# Revit family: Geberit Bambini WC sedište za decu_PRO_450219
name_source: partatom
category: Furniture
revit_build: Autodesk Revit 2018 (Build: 20190510_1515(x64)
units: mm (PartAtom-declared; Revit-internal decimal feet)

## family parameters
Always vertical = Yes
Cut with Voids When Loaded = No
OmniClass Number = 23.40.20.21
OmniClass Title = Toilet and Bath Specialties
Room Calculation Point = Yes
Shared = No
Work Plane-Based = No

## types (2) — shared parameters
BIM datoteka, datum izmene = 2020.05.18
BIM datoteka, proizvođač = Geberit
BIM datoteka, verzija = GEB MG 1.2
CW Connection = Yes
Description = Geberit Bambini WC sedište za decu
GEB_culture = sr-RS
GEB_generic_description = GBC
GEB_generic_manufacturer = generic
GEB_pimversion = 22.02.12
GEB_processing_type = T
GEB_reference = PRO_450219
GEB_translations = {"ATT_10673":"EAN code basic data","ATT_459792":"Boja / površina","applicationPurposes":"Namene","application_range":"Oblast primene","brandName":"Robna marka","characteristics":"Svojstva","content_creator":"BIM datoteka, proizvođač","content_date_changed":"BIM datoteka, datum izmene","content_version":"BIM datoteka, verzija","key 1000":"Broj artikla","name":"Naziv","productBrand":"Robna marka proizvoda","scopeOfDelivery":"Obim isporuke","type":"Tip","fixed_material":"Osnovni materijal"}
HW Connection = No
IfcDescription = Geberit Bambini WC sedište za decu
IfcExportAs = IfcSanitaryTerminal
IfcExportType = WCSEAT
LOD300 = No
LOD400 = Yes
Manufacturer = Geberit
Namene = Za dečije toalete
Naziv = Geberit Bambini WC sedište za decu
Obim isporuke = WC sedište
Oblast primene = Furniture
Osnovni materijal = Geberit, Plastic, Opaque white
Robna marka = Geberit
Vent Connection = No
Waste Connection = Yes

## per-type parameters (varying)
| type | 573334000_0_0_view | 573334000_0_1_view | Boja / površina | Broj artikla | EAN code basic data |
| 573334000 Geberit Bambini WC sedište za decu | Yes | No | bela | 573334000 | 4022009163063 |
| 573337000 Geberit Bambini WC sedište za decu | No | Yes | rubincrvena | 573337000 | 4022009163070 |

## geometry (parser evidence)
native form markers: Blend x8, Sweep x22
no freeform markers — native parametric forms only
